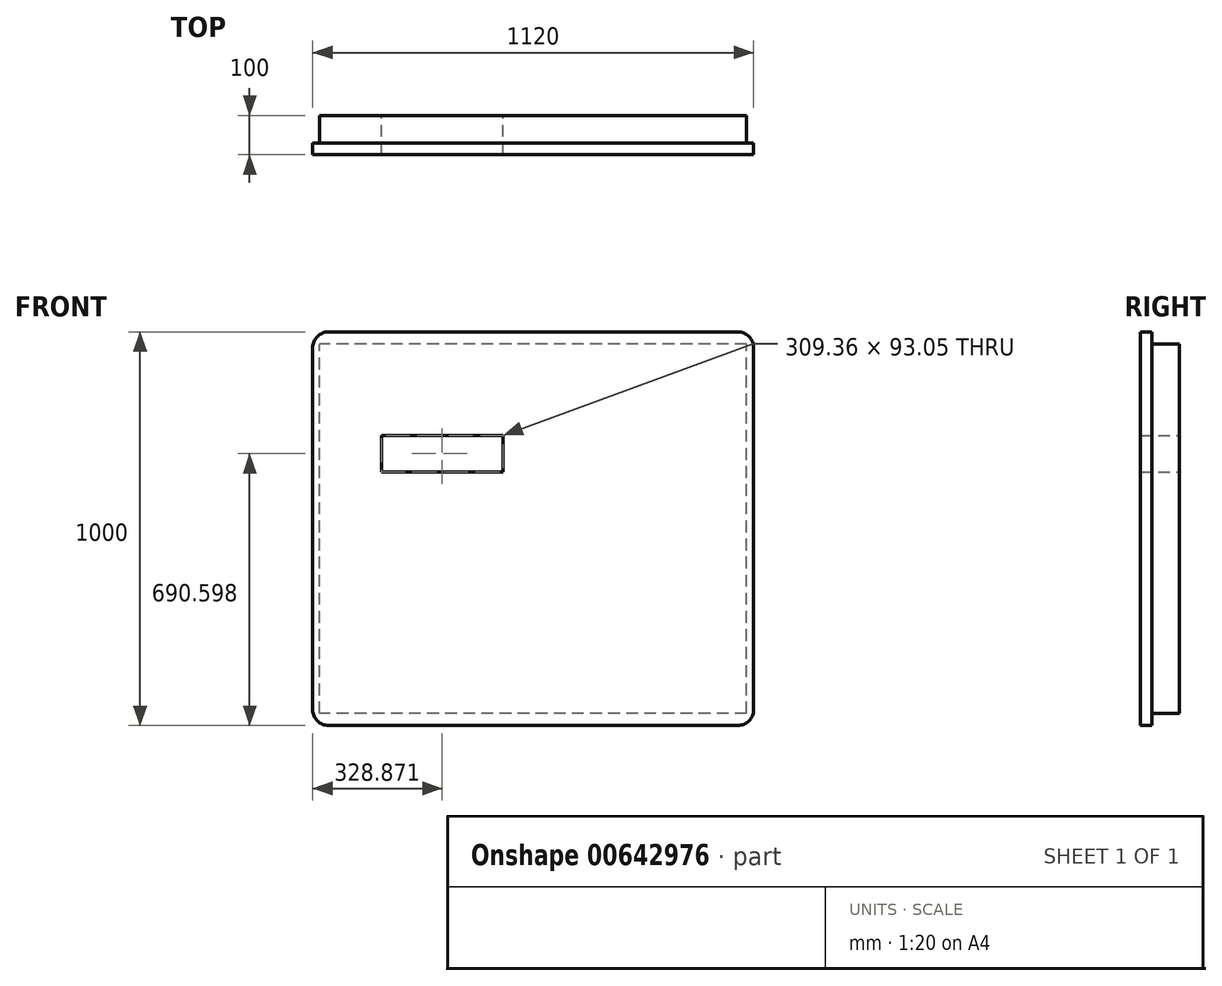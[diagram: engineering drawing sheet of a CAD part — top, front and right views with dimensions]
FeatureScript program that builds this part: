
annotation { "Feature Type Name" : "Feature", "Feature Type Description" : "" }
export const myFeature = defineFeature(function(context is Context, id is Id, definition is map)
    precondition{}
    {
        {
            var Q0;
            Q0=qCreatedBy(makeId("Front.planeOp"),FACE);
            var sketch = newSketch(context, id + "F0", { "sketchPlane" : qUnion([Q0])});
            skLineSegment(sketch, "E0.bottom", {"start": v(542.5, -469) * mm, "end": v(-542.5, -469) * mm});
            skLineSegment(sketch, "E0.top", {"start": v(542.5, 469) * mm, "end": v(-542.5, 469) * mm});
            skLineSegment(sketch, "E0.left", {"start": v(542.5, -469) * mm, "end": v(542.5, 469) * mm});
            skLineSegment(sketch, "E0.right", {"start": v(-542.5, -469) * mm, "end": v(-542.5, 469) * mm});
            skPoint(sketch, "E0.middle", {"position": v(0, 0) * mm});
            skSolve(sketch);
        }
        {
            var Q0;
            Q0 = qSketchRegion(id + "F0", true);
            extrude(context, id + "F1", {"entities" : qUnion([Q0]), "depth" : 70 * mm, "offsetDistance" : 25 * mm});
        }
        {
            var Q0;
            Q0=makeQuery(id+"F1.opExtrude","CAP_FACE",FACE,{"disambiguationData":[OSD([sQuery(id+"F0.wireOp",EDGE,"E0.bottom"),sQuery(id+"F0.wireOp",EDGE,"E0.top"),sQuery(id+"F0.wireOp",EDGE,"E0.left"),sQuery(id+"F0.wireOp",EDGE,"E0.right")])],"isStart":false});
            var sketch = newSketch(context, id + "F2", { "sketchPlane" : qUnion([Q0])});
            skLineSegment(sketch, "E1.bottom", {"start": v(560, -500) * mm, "end": v(-560, -500) * mm});
            skLineSegment(sketch, "E1.top", {"start": v(560, 500) * mm, "end": v(-560, 500) * mm});
            skLineSegment(sketch, "E1.left", {"start": v(560, -500) * mm, "end": v(560, 500) * mm});
            skLineSegment(sketch, "E1.right", {"start": v(-560, -500) * mm, "end": v(-560, 500) * mm});
            skPoint(sketch, "E1.middle", {"position": v(0, 0) * mm});
            skSolve(sketch);
        }
        {
            var Q0;
            Q0=makeQuery(id+"F2.imprint","IMPRINT",FACE,{"disambiguationData":[TD([[makeQuery(id+"F2.imprint","IMPRINT",EDGE,{"derivedFrom":sQuery(id+"F2.wireOp",EDGE,"E1.bottom")}),-1.0]])]});
            var Q1;
            Q1=makeQuery(id+"F2.imprint","IMPRINT",FACE,{"disambiguationData":[TD([[makeQuery(id+"F2.imprint","IMPRINT",EDGE,{"derivedFrom":makeQuery(id+"F1.opExtrude","CAP_EDGE",EDGE,{"disambiguationData":[OSD([sQuery(id+"F0.wireOp",EDGE,"E0.bottom")])],"isStart":false})}),-1.0]])]});
            extrude(context, id + "F3", {"entities" : qUnion([Q0, Q1]), "operationType" : NewBodyOperationType.ADD, "depth" : 30 * mm, "offsetDistance" : 25 * mm});
        }
        {
            var Q0;
            Q0=makeQuery(id+"F1.opExtrude","CAP_FACE",FACE,{"disambiguationData":[OSD([sQuery(id+"F0.wireOp",EDGE,"E0.bottom"),sQuery(id+"F0.wireOp",EDGE,"E0.top"),sQuery(id+"F0.wireOp",EDGE,"E0.left"),sQuery(id+"F0.wireOp",EDGE,"E0.right")])],"isStart":true});
            var sketch = newSketch(context, id + "F4", { "sketchPlane" : qUnion([Q0])});
            skLineSegment(sketch, "E2.bottom", {"start": v(76.45, 237.12) * mm, "end": v(385.8, 237.12) * mm});
            skLineSegment(sketch, "E2.top", {"start": v(76.45, 144.07) * mm, "end": v(385.8, 144.07) * mm});
            skLineSegment(sketch, "E2.left", {"start": v(76.45, 237.12) * mm, "end": v(76.45, 144.07) * mm});
            skLineSegment(sketch, "E2.right", {"start": v(385.8, 237.12) * mm, "end": v(385.8, 144.07) * mm});
            skSolve(sketch);
        }
        {
            var Q0;
            Q0=makeQuery(id+"F4.imprint","IMPRINT",FACE,{"disambiguationData":[TD([[makeQuery(id+"F4.imprint","IMPRINT",EDGE,{"derivedFrom":sQuery(id+"F4.wireOp",EDGE,"E2.bottom")}),-1.0]])]});
            extrude(context, id + "F5", {"entities" : qUnion([Q0]), "operationType" : NewBodyOperationType.REMOVE, "oppositeDirection" : true, "depth" : 300 * mm, "offsetDistance" : 25 * mm});
        }
        {
            var Q0;
            Q0=makeQuery(id+"F3.opExtrude","SWEPT_EDGE",EDGE,{"disambiguationData":[OSD([sQuery(id+"F2.wireOp",EDGE,"E1.top"),sQuery(id+"F2.wireOp",EDGE,"E1.right")])]});
            var Q1;
            Q1=makeQuery(id+"F3.opExtrude","SWEPT_EDGE",EDGE,{"disambiguationData":[OSD([sQuery(id+"F2.wireOp",EDGE,"E1.top"),sQuery(id+"F2.wireOp",EDGE,"E1.left")])]});
            var Q2;
            Q2=makeQuery(id+"F3.opExtrude","SWEPT_EDGE",EDGE,{"disambiguationData":[OSD([sQuery(id+"F2.wireOp",EDGE,"E1.bottom"),sQuery(id+"F2.wireOp",EDGE,"E1.left")])]});
            var Q3;
            Q3=makeQuery(id+"F3.opExtrude","SWEPT_EDGE",EDGE,{"disambiguationData":[OSD([sQuery(id+"F2.wireOp",EDGE,"E1.bottom"),sQuery(id+"F2.wireOp",EDGE,"E1.right")])]});
            fillet(context, id + "F6", {"entities" : qUnion([Q0, Q1, Q2, Q3]), "radius" : 40 * mm, "tangentPropagation" : true, "allowEdgeOverflow" : false});
        }
    });
